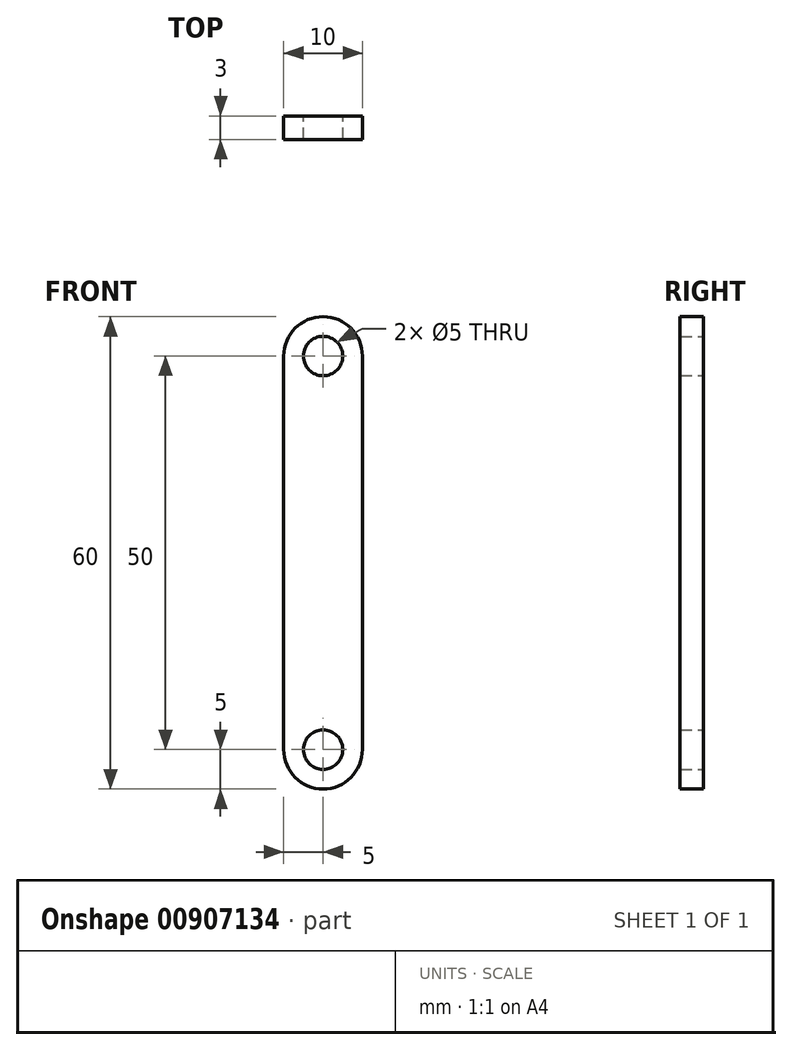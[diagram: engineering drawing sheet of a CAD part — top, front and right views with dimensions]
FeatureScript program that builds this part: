
annotation { "Feature Type Name" : "Feature", "Feature Type Description" : "" }
export const myFeature = defineFeature(function(context is Context, id is Id, definition is map)
    precondition{}
    {
        {
            var Q0;
            Q0=qCreatedBy(makeId("Front.planeOp"),FACE);
            var sketch = newSketch(context, id + "F0", { "sketchPlane" : qUnion([Q0])});
            skLineSegment(sketch, "E0.left", {"start": v(5, 25) * mm, "end": v(5, -25) * mm});
            skLineSegment(sketch, "E0.right", {"start": v(-5, 25) * mm, "end": v(-5, -25) * mm});
            skPoint(sketch, "E0.middle", {"position": v(0, 0) * mm});
            skArc(sketch, "E1", {"start": v(5, 25) * mm, "mid": v(0, 30) * mm, "end": v(-5, 25) * mm});
            skArc(sketch, "E2", {"start": v(-5, -25) * mm, "mid": v(0, -30) * mm, "end": v(5, -25) * mm});
            skCircle(sketch, "E3", {"center": v(0, 25) * mm, "radius": 2.5 * mm});
            skCircle(sketch, "E4", {"center": v(0, -25) * mm, "radius": 2.5 * mm});
            skSolve(sketch);
        }
        {
            var Q0;
            Q0=qSketchRegion(id+"F0",true);
            extrude(context, id + "F1", {"entities" : qUnion([Q0]), "depth" : 3 * mm, "offsetDistance" : 25 * mm});
        }
    });
